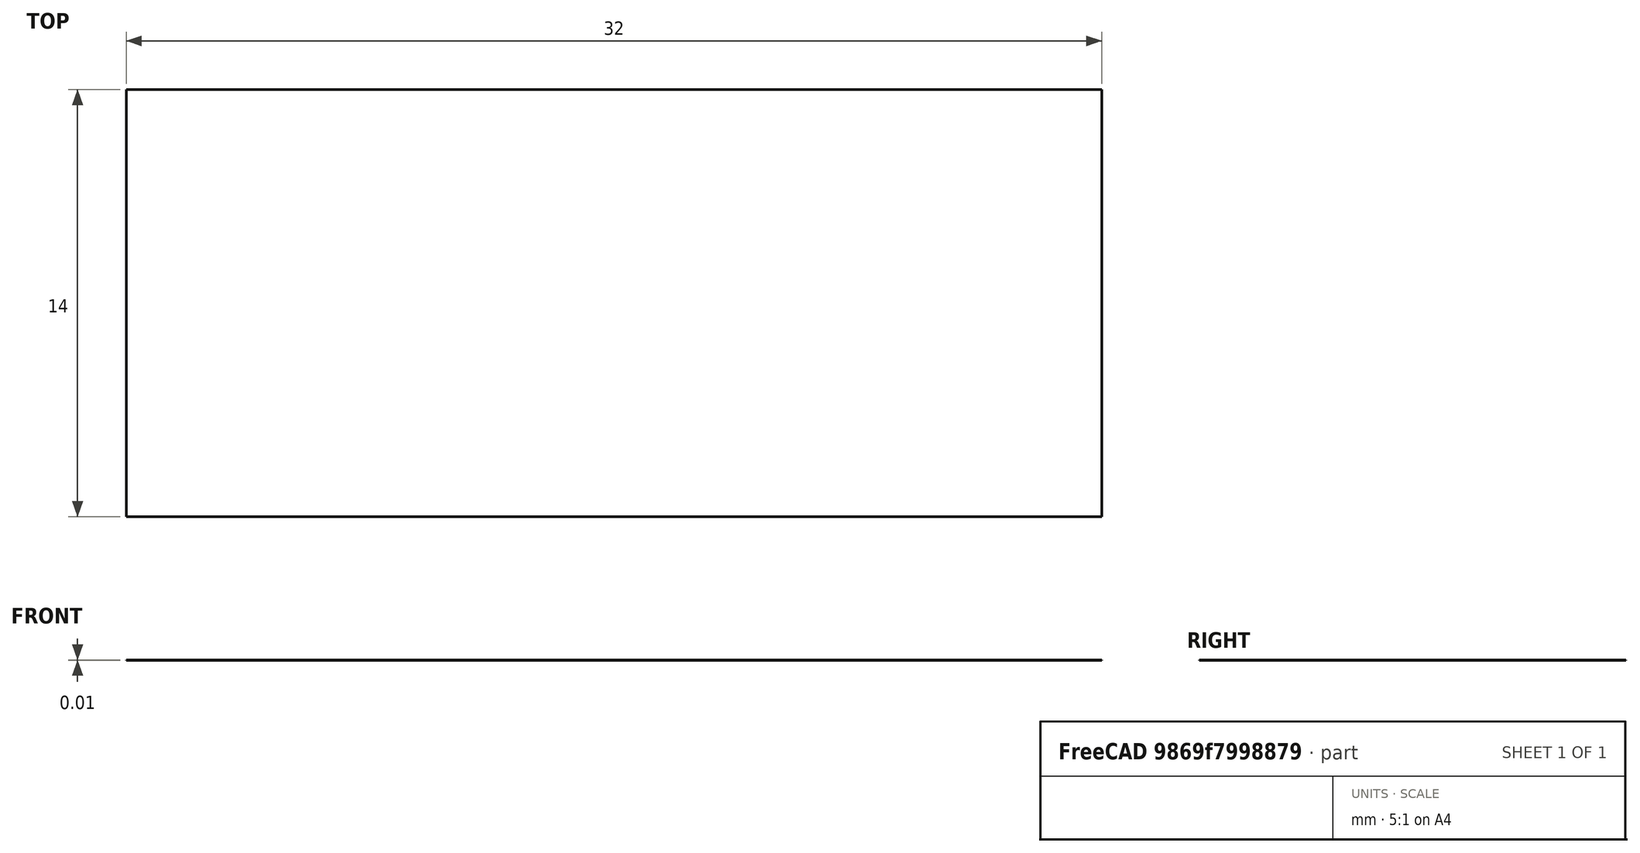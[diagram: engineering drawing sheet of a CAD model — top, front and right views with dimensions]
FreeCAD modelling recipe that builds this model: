
FCSTD DOCUMENT  (FreeCAD 0.19R23058 (Git))
Label: label_2
License: All rights reserved
LicenseURL: http://en.wikipedia.org/wiki/All_rights_reserved
objects: App::MaterialObjectPython×1, Part::Box×1, App::DocumentObjectGroupPython×1, App::FeaturePython×1
note: 1 computed .brp shape members not serialized (recipe doc carries the construction recipe); baked Part::Feature solids carry a one-line shape summary decoded from their .brp

FEATURE [App::MaterialObjectPython] Material  label="Aluminum 6061-T6"  # material (typed FeaturePython)
  Description = Precipitation-hardened, Nonferrous Aluminum alloy
  Material = AuthorAndLicense=Aluminum-6061-T6; CardName=Aluminum-6061-T6; Color=(0.8, 0.8, 0.8, 1.0); Density=2700 kg/m^3; Description=Precipitation-hardened, Nonferrous Aluminum alloy; DiffuseColor=(0.8, 0.8, 0.8, 1.0); Father=Metal; KindOfMaterial=Aluminium; KindOfMaterialDE=Aluminium; Name=Aluminum 6061-T6; PoissonRatio=0.33; ProductURL=https://en.wikipedia.org/wiki/6061_aluminium_alloy; SectionColor=(0.8, 0.8, 0.8, 1.0); ThermalConductivity=167 W/m/K; Transparency=0; UltimateTensileStrength=310 MPa; ViewColor=(0.8, 0.8, 0.8, 1.0); YoungsModulus=69000 MPa
  ProductURL = https://en.wikipedia.org/wiki/6061_aluminium_alloy
  Transparency = 0
FEATURE [Part::Box] Box  label="Куб"
  AttacherType = Attacher::AttachEngine3D
  Height = 0.01
  Length = 32
  Material = -> Material
  Width = 14
FEATURE [App::DocumentObjectGroupPython] MaterialContainer  label="Materials"  # scripted group (container) (typed FeaturePython)
  Group = -> [Material]
FEATURE [App::FeaturePython] TextureConfig  # WARN: FeaturePython — macro-defined, semantics opaque (R4)
